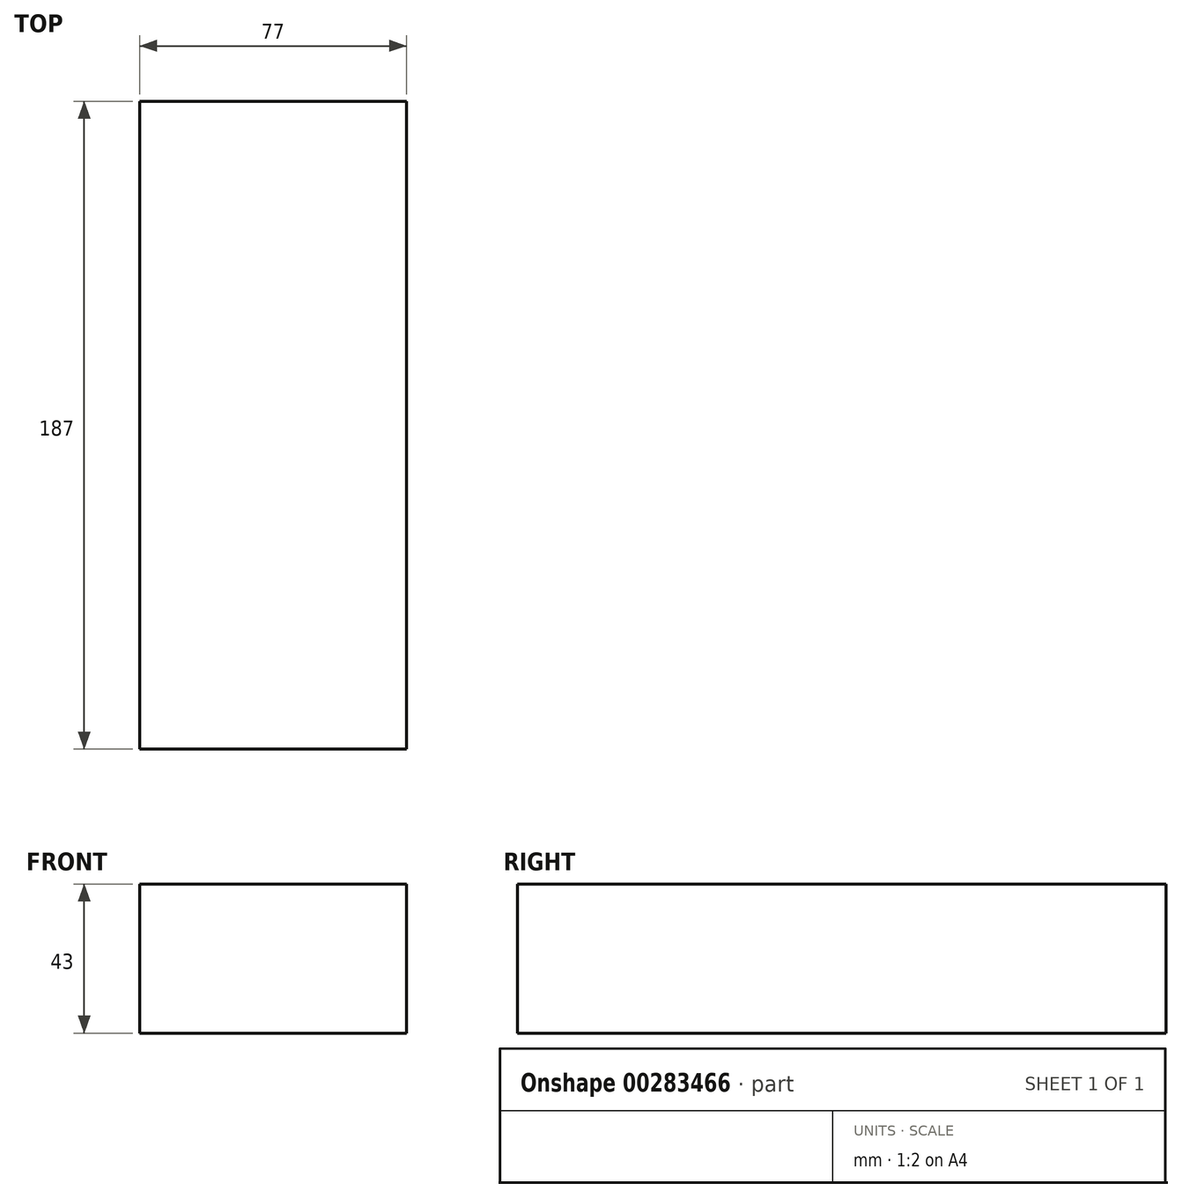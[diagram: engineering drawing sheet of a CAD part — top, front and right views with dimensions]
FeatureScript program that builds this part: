
annotation { "Feature Type Name" : "Feature", "Feature Type Description" : "" }
export const myFeature = defineFeature(function(context is Context, id is Id, definition is map)
    precondition{}
    {
        {
            var Q0;
            Q0=qCreatedBy(makeId("Right.planeOp"),FACE);
            var sketch = newSketch(context, id + "F0", { "sketchPlane" : qUnion([Q0])});
            skLineSegment(sketch, "E0.bottom", {"start": v(0, 0) * mm, "end": v(-187, 0) * mm});
            skLineSegment(sketch, "E0.top", {"start": v(0, 43) * mm, "end": v(-187, 43) * mm});
            skLineSegment(sketch, "E0.left", {"start": v(0, 0) * mm, "end": v(0, 43) * mm});
            skLineSegment(sketch, "E0.right", {"start": v(-187, 0) * mm, "end": v(-187, 43) * mm});
            skSolve(sketch);
        }
        {
            var Q0;
            Q0=makeQuery(id+"F0.imprint","IMPRINT",FACE,{"disambiguationData":[TD([[makeQuery(id+"F0.imprint","IMPRINT",EDGE,{"derivedFrom":sQuery(id+"F0.wireOp",EDGE,"E0.bottom")}),-1.0]])]});
            extrude(context, id + "F1", {"entities" : qUnion([Q0]), "depth" : 77 * mm});
        }
    });
